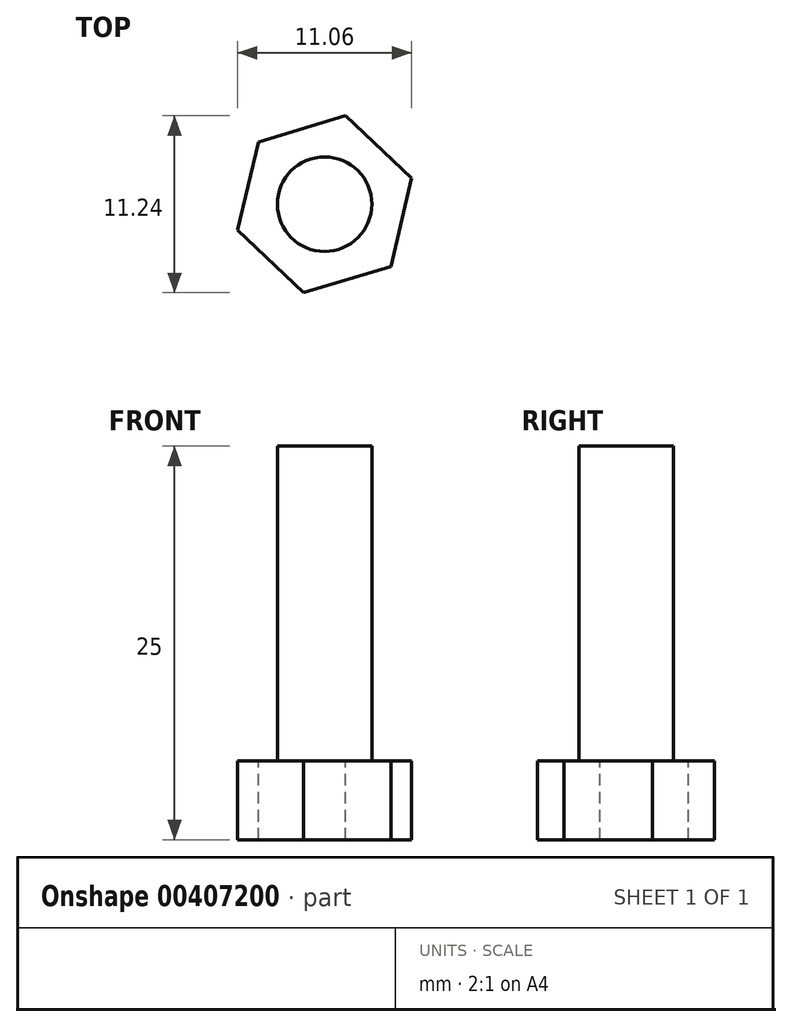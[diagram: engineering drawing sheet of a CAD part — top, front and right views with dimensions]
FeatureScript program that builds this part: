
annotation { "Feature Type Name" : "Feature", "Feature Type Description" : "" }
export const myFeature = defineFeature(function(context is Context, id is Id, definition is map)
    precondition{}
    {
        {
            var Q0;
            Q0=qCreatedBy(makeId("Top.planeOp"),FACE);
            var sketch = newSketch(context, id + "F0", { "sketchPlane" : qUnion([Q0])});
            skCircle(sketch, "E0", {"center": v(0, 0) * mm, "radius": 3 * mm});
            skSolve(sketch);
        }
        {
            var Q0;
            Q0=makeQuery(id+"F0.imprint","IMPRINT",FACE,{"disambiguationData":[TD([[makeQuery(id+"F0.imprint","IMPRINT",EDGE,{"derivedFrom":sQuery(id+"F0.wireOp",EDGE,"E0")}),1.0]])]});
            extrude(context, id + "F1", {"entities" : qUnion([Q0]), "depth" : 20 * mm});
        }
        {
            var Q0;
            Q0=makeQuery(id+"F1.opExtrude","CAP_FACE",FACE,{"disambiguationData":[OSD([sQuery(id+"F0.wireOp",EDGE,"E0")])],"isStart":true});
            var sketch = newSketch(context, id + "F2", { "sketchPlane" : qUnion([Q0])});
            skCircle(sketch, "E1", {"center": v(0, 0) * mm, "radius": 5 * mm, "construction": true});
            skLineSegment(sketch, "E2.0", {"start": v(5.53, -1.66) * mm, "end": v(1.33, -5.62) * mm});
            skLineSegment(sketch, "E2.1", {"start": v(1.33, -5.62) * mm, "end": v(-4.2, -3.96) * mm});
            skLineSegment(sketch, "E2.2", {"start": v(-4.2, -3.96) * mm, "end": v(-5.53, 1.66) * mm});
            skLineSegment(sketch, "E2.3", {"start": v(-5.53, 1.66) * mm, "end": v(-1.33, 5.62) * mm});
            skLineSegment(sketch, "E2.4", {"start": v(-1.33, 5.62) * mm, "end": v(4.2, 3.96) * mm});
            skLineSegment(sketch, "E2.5", {"start": v(4.2, 3.96) * mm, "end": v(5.53, -1.66) * mm});
            skPoint(sketch, "E2.0.midPoint", {"position": v(3.43, -3.64) * mm});
            skSolve(sketch);
        }
        {
            var Q0;
            Q0=makeQuery(id+"F2.imprint","IMPRINT",FACE,{"disambiguationData":[TD([[makeQuery(id+"F2.imprint","IMPRINT",EDGE,{"derivedFrom":sQuery(id+"F2.wireOp",EDGE,"E2.0")}),-1.0]])]});
            var Q1;
            Q1=makeQuery(id+"F2.imprint","IMPRINT",FACE,{"disambiguationData":[TD([[makeQuery(id+"F2.imprint","IMPRINT",EDGE,{"derivedFrom":makeQuery(id+"F1.opExtrude","CAP_EDGE",EDGE,{"disambiguationData":[OSD([sQuery(id+"F0.wireOp",EDGE,"E0")])],"isStart":true})}),-1.0]])]});
            extrude(context, id + "F3", {"entities" : qUnion([Q0, Q1]), "operationType" : NewBodyOperationType.ADD, "depth" : 5 * mm});
        }
    });
